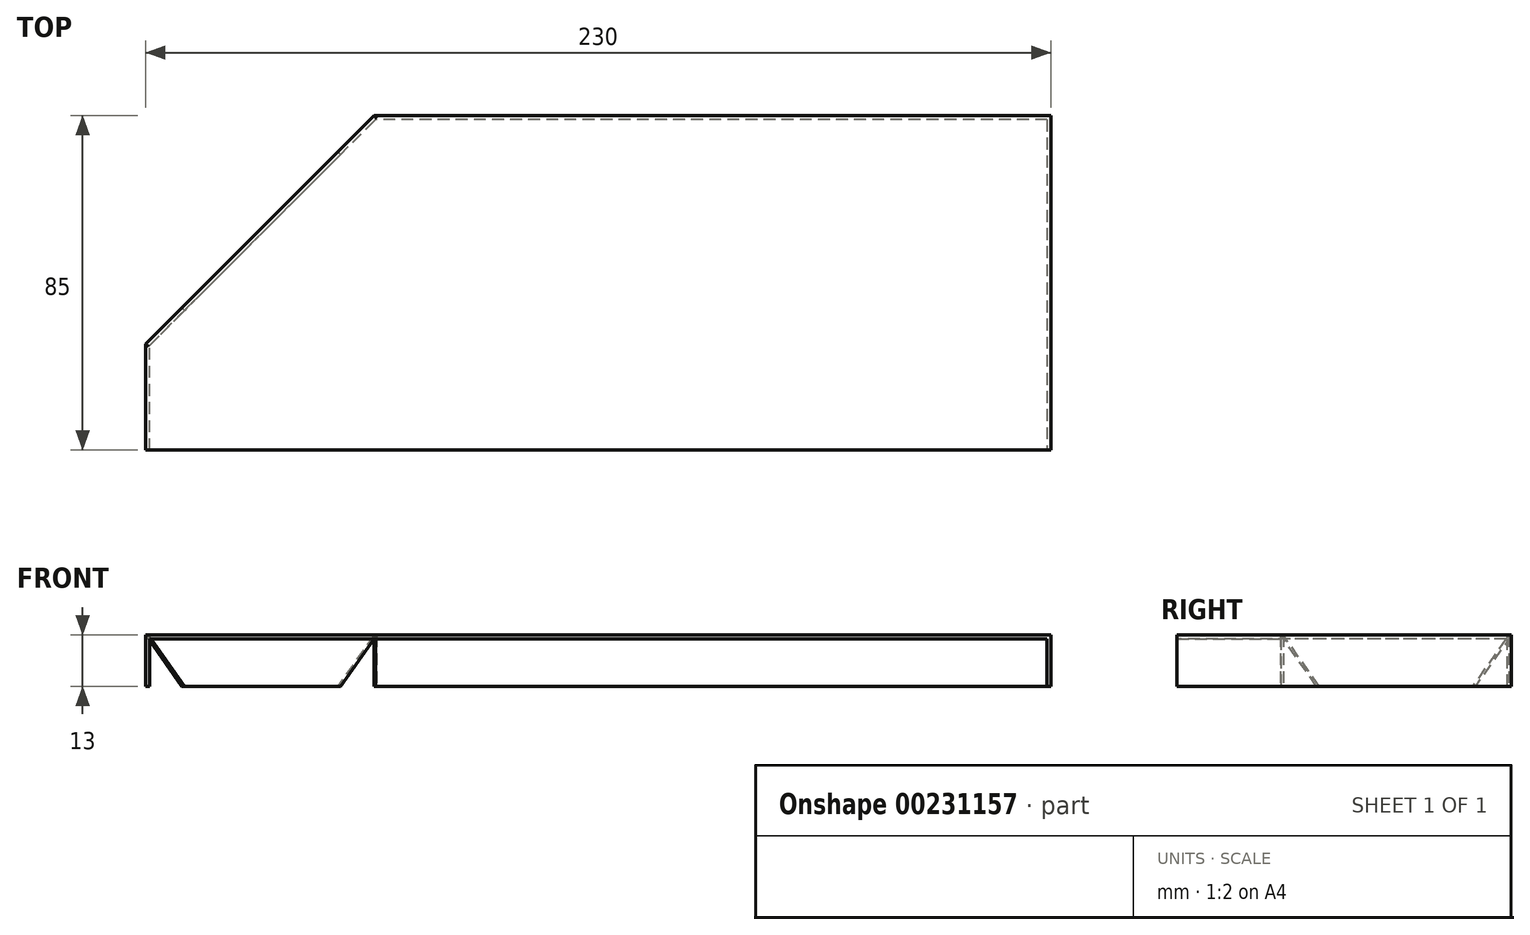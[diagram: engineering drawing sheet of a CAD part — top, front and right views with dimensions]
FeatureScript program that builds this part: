
annotation { "Feature Type Name" : "Feature", "Feature Type Description" : "" }
export const myFeature = defineFeature(function(context is Context, id is Id, definition is map)
    precondition{}
    {
        {
            var Q0;
            Q0=qCreatedBy(makeId("Top.planeOp"),FACE);
            var sketch = newSketch(context, id + "F0", { "sketchPlane" : qUnion([Q0])});
            skLineSegment(sketch, "E0.bottom", {"start": v(115, -42.5) * mm, "end": v(-115, -42.5) * mm});
            skLineSegment(sketch, "E0.top", {"start": v(115, 42.5) * mm, "end": v(-57, 42.5) * mm});
            skLineSegment(sketch, "E0.left", {"start": v(115, -42.5) * mm, "end": v(115, 42.5) * mm});
            skLineSegment(sketch, "E0.right", {"start": v(-115, -42.5) * mm, "end": v(-115, -15.5) * mm});
            skPoint(sketch, "E0.middle", {"position": v(0, 0) * mm});
            skLineSegment(sketch, "E1", {"start": v(-115, -15.5) * mm, "end": v(-57, 42.5) * mm});
            skPoint(sketch, "E2.orphan", {"position": v(-115, 42.5) * mm});
            skSolve(sketch);
        }
        {
            var Q0;
            Q0 = qSketchRegion(id + "F0", true);
            extrude(context, id + "F1", {"entities" : qUnion([Q0]), "depth" : 1 * mm});
        }
        {
            var Q0;
            Q0=makeQuery(id+"F1.opExtrude","CAP_FACE",FACE,{"disambiguationData":[OSD([sQuery(id+"F0.wireOp",EDGE,"E0.bottom"),sQuery(id+"F0.wireOp",EDGE,"E0.top"),sQuery(id+"F0.wireOp",EDGE,"E0.left"),sQuery(id+"F0.wireOp",EDGE,"E0.right"),sQuery(id+"F0.wireOp",EDGE,"E1")])],"isStart":true});
            var sketch = newSketch(context, id + "F2", { "sketchPlane" : qUnion([Q0])});
            skLineSegment(sketch, "E3", {"start": v(-115, 15.5) * mm, "end": v(-115, 42.5) * mm});
            skLineSegment(sketch, "E4", {"start": v(-57, -42.5) * mm, "end": v(-115, 15.5) * mm});
            skLineSegment(sketch, "E5", {"start": v(-57, -42.5) * mm, "end": v(115, -42.5) * mm});
            skLineSegment(sketch, "E6", {"start": v(115, 42.5) * mm, "end": v(115, -42.5) * mm});
            skLineSegment(sketch, "E7", {"start": v(115, 42.5) * mm, "end": v(114, 42.5) * mm});
            skLineSegment(sketch, "E8", {"start": v(114, -41.5) * mm, "end": v(114, 42.5) * mm});
            skLineSegment(sketch, "E9", {"start": v(114, -41.5) * mm, "end": v(-56.59, -41.5) * mm});
            skLineSegment(sketch, "E10", {"start": v(-114, 42.5) * mm, "end": v(-114, 15.91) * mm});
            skLineSegment(sketch, "E11", {"start": v(-114, 42.5) * mm, "end": v(-115, 42.5) * mm});
            skLineSegment(sketch, "E12", {"start": v(-56.59, -41.5) * mm, "end": v(-114, 15.91) * mm});
            skSolve(sketch);
        }
        {
            var Q0;
            Q0 = qSketchRegion(id + "F2", true);
            extrude(context, id + "F3", {"entities" : qUnion([Q0]), "operationType" : NewBodyOperationType.ADD, "depth" : 12 * mm});
        }
        {
            var Q0;
            Q0=makeQuery(id+"F3.boolean.opBoolean","MERGE",FACE,{"derivedFrom":[makeQuery(id+"F1.opExtrude","SWEPT_FACE",FACE,{"disambiguationData":[OSD([sQuery(id+"F0.wireOp",EDGE,"E1")])]}),makeQuery(id+"F3.opExtrude","SWEPT_FACE",FACE,{"disambiguationData":[OSD([sQuery(id+"F2.wireOp",EDGE,"E4")])]})]});
            var sketch = newSketch(context, id + "F4", { "sketchPlane" : qUnion([Q0])});
            skLineSegment(sketch, "E13", {"start": v(10.25, 1) * mm, "end": v(10.26, 1) * mm});
            skLineSegment(sketch, "E14", {"start": v(10.26, 1) * mm, "end": v(23.26, -12) * mm});
            skLineSegment(sketch, "E15", {"start": v(23.26, -12) * mm, "end": v(10.25, -12) * mm});
            skLineSegment(sketch, "E16", {"start": v(10.25, -12) * mm, "end": v(10.25, 1) * mm});
            skLineSegment(sketch, "E17", {"start": v(92.28, 1) * mm, "end": v(92.28, -12) * mm});
            skLineSegment(sketch, "E18", {"start": v(92.28, -12) * mm, "end": v(79.27, -12) * mm});
            skLineSegment(sketch, "E19", {"start": v(79.27, -12) * mm, "end": v(92.27, 1) * mm});
            skLineSegment(sketch, "E20", {"start": v(92.27, 1) * mm, "end": v(92.28, 1) * mm});
            skSolve(sketch);
        }
        {
            var Q0;
            Q0 = qSketchRegion(id + "F4", true);
            extrude(context, id + "F5", {"entities" : qUnion([Q0]), "operationType" : NewBodyOperationType.REMOVE, "oppositeDirection" : true, "depth" : 1 * mm});
        }
    });
